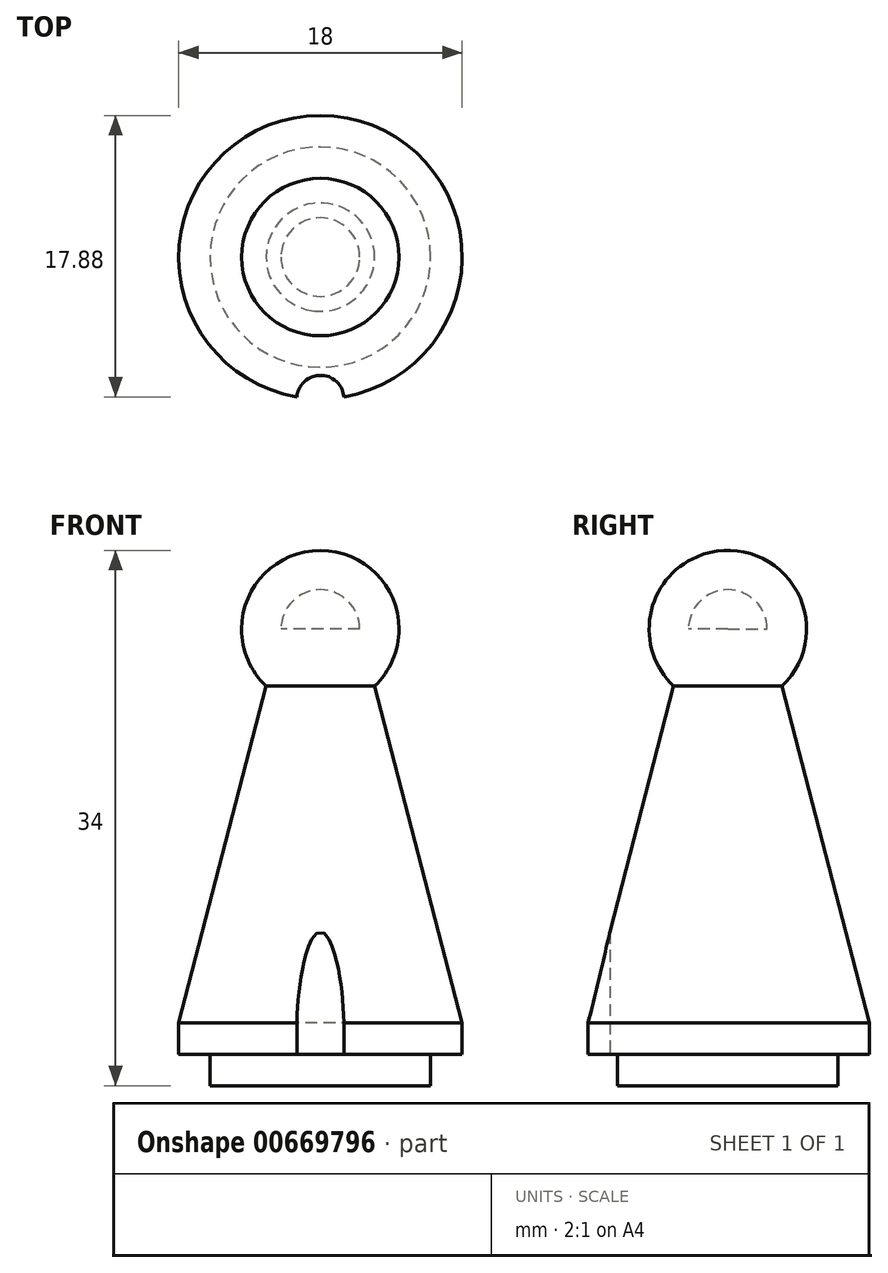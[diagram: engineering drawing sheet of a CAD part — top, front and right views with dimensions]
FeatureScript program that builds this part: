
annotation { "Feature Type Name" : "Feature", "Feature Type Description" : "" }
export const myFeature = defineFeature(function(context is Context, id is Id, definition is map)
    precondition{}
    {
        {
            var Q0;
            Q0=qCreatedBy(makeId("Top.planeOp"),FACE);
            var sketch = newSketch(context, id + "F0", { "sketchPlane" : qUnion([Q0])});
            skCircle(sketch, "E0", {"center": v(0, 0) * mm, "radius": 7 * mm});
            skSolve(sketch);
        }
        {
            var Q0;
            Q0 = qSketchRegion(id + "F0", true);
            extrude(context, id + "F1", {"entities" : qUnion([Q0]), "depth" : 2 * mm, "offsetDistance" : 25 * mm});
        }
        {
            var Q0;
            Q0=makeQuery(id+"F1.opExtrude","CAP_FACE",FACE,{"disambiguationData":[OSD([sQuery(id+"F0.wireOp",EDGE,"E0")])],"isStart":false});
            var sketch = newSketch(context, id + "F2", { "sketchPlane" : qUnion([Q0])});
            skCircle(sketch, "E1", {"center": v(0, 0) * mm, "radius": 9 * mm});
            skSolve(sketch);
        }
        {
            var Q0;
            Q0 = qSketchRegion(id + "F2", true);
            extrude(context, id + "F3", {"entities" : qUnion([Q0]), "operationType" : NewBodyOperationType.ADD, "depth" : 2 * mm, "offsetDistance" : 25 * mm});
        }
        {
            var Q0;
            Q0=makeQuery(id+"F3.opExtrude","CAP_FACE",FACE,{"disambiguationData":[OSD([sQuery(id+"F2.wireOp",EDGE,"E1")])],"isStart":false});
            cPlane(context, id + "F4", {"entities" : qUnion([Q0]), "cplaneType" : CPlaneType.OFFSET, "offset" : 25 * mm, "width" : 150 * mm, "height" : 150 * mm});
        }
        {
            var Q0;
            Q0=qCreatedBy(id+"F4.planeOp",FACE);
            var sketch = newSketch(context, id + "F5", { "sketchPlane" : qUnion([Q0])});
            skCircle(sketch, "E2", {"center": v(0, 0) * mm, "radius": 2.5 * mm});
            skSolve(sketch);
        }
        {
            var Q1;
            Q1=makeQuery(id+"F5.imprint","IMPRINT",FACE,{"disambiguationData":[TD([[makeQuery(id+"F5.imprint","IMPRINT",EDGE,{"derivedFrom":sQuery(id+"F5.wireOp",EDGE,"E2")}),1.0]])]});
            var Q2;
            Q2=makeQuery(id+"F3.opExtrude","CAP_FACE",FACE,{"disambiguationData":[OSD([sQuery(id+"F2.wireOp",EDGE,"E1")])],"isStart":false});
            loft(context, id + "F6", {"operationType" : NewBodyOperationType.ADD, "sheetProfilesArray" : [{ "sheetProfileEntities" : qUnion([Q1]) }, { "sheetProfileEntities" : qUnion([Q2]) }]});
        }
        {
            var Q0;
            Q0=makeQuery(id+"F6.opLoft","CAP_FACE",FACE,{"disambiguationData":[OSD([makeQuery(id+"F5.imprint","IMPRINT",FACE,{"disambiguationData":[TD([[makeQuery(id+"F5.imprint","IMPRINT",EDGE,{"derivedFrom":sQuery(id+"F5.wireOp",EDGE,"E2")}),1.0]])]})])],"isStart":true});
            var sketch = newSketch(context, id + "F7", { "sketchPlane" : qUnion([Q0])});
            skCircle(sketch, "E3", {"center": v(0, 0) * mm, "radius": 5 * mm});
            skLineSegment(sketch, "E4", {"start": v(-5, 0) * mm, "end": v(5, 0) * mm});
            skSolve(sketch);
        }
        {
            var Q0;
            {var subQ0=sQuery(id+"F7.wireOp",EDGE,"E4");var subQ1=sQuery(id+"F7.wireOp",EDGE,"E3");var subQ2=makeQuery(id+"F7.imprint","INTERSECT",VERTEX,{"disambiguationData":[OD(0.0)],"derivedFrom":[subQ1,subQ0]});Q0=makeQuery(id+"F7.imprint","IMPRINT",FACE,{"disambiguationData":[TD([[makeQuery(id+"F7.imprint","IMPRINT",EDGE,{"disambiguationData":[TD([[subQ2,-1.0]])],"derivedFrom":subQ1}),1.0]])]});}
            var Q1;
            Q1=sQuery(id+"F7.wireOp",EDGE,"E4");
            revolve(context, id + "F8", {"operationType" : NewBodyOperationType.ADD, "entities" : qUnion([Q0]), "axis" : qUnion([Q1]), "revolveType" : RevolveType.FULL});
        }
        {
            var Q0;
            Q0=makeQuery(id+"F3.opExtrude","CAP_FACE",FACE,{"disambiguationData":[OSD([sQuery(id+"F2.wireOp",EDGE,"E1")])],"isStart":true});
            var sketch = newSketch(context, id + "F9", { "sketchPlane" : qUnion([Q0])});
            skCircle(sketch, "E5", {"center": v(0, 9) * mm, "radius": 1.5 * mm});
            skSolve(sketch);
        }
        {
            var Q0;
            {var subQ0=sQuery(id+"F9.wireOp",EDGE,"E5");var subQ1=makeQuery(id+"F3.opExtrude","CAP_EDGE",EDGE,{"disambiguationData":[OSD([sQuery(id+"F2.wireOp",EDGE,"E1")])],"isStart":true});var subQ2=makeQuery(id+"F9.imprint","INTERSECT",VERTEX,{"disambiguationData":[OD(0.0)],"derivedFrom":[subQ1,subQ0]});Q0=makeQuery(id+"F9.imprint","IMPRINT",FACE,{"disambiguationData":[TD([[makeQuery(id+"F9.imprint","IMPRINT",EDGE,{"disambiguationData":[TD([[subQ2,1.0]])],"derivedFrom":subQ0}),1.0]])]});}
            var Q1;
            {var subQ0=sQuery(id+"F9.wireOp",EDGE,"E5");var subQ1=makeQuery(id+"F3.opExtrude","CAP_EDGE",EDGE,{"disambiguationData":[OSD([sQuery(id+"F2.wireOp",EDGE,"E1")])],"isStart":true});var subQ2=makeQuery(id+"F9.imprint","INTERSECT",VERTEX,{"disambiguationData":[OD(0.0)],"derivedFrom":[subQ1,subQ0]});Q1=makeQuery(id+"F9.imprint","IMPRINT",FACE,{"disambiguationData":[TD([[makeQuery(id+"F9.imprint","IMPRINT",EDGE,{"disambiguationData":[TD([[subQ2,-1.0]])],"derivedFrom":subQ0}),1.0]])]});}
            extrude(context, id + "F10", {"entities" : qUnion([Q0, Q1]), "operationType" : NewBodyOperationType.REMOVE, "endBound" : BoundingType.THROUGH_ALL, "oppositeDirection" : true, "depth" : 25 * mm, "offsetDistance" : 25 * mm});
        }
    });
